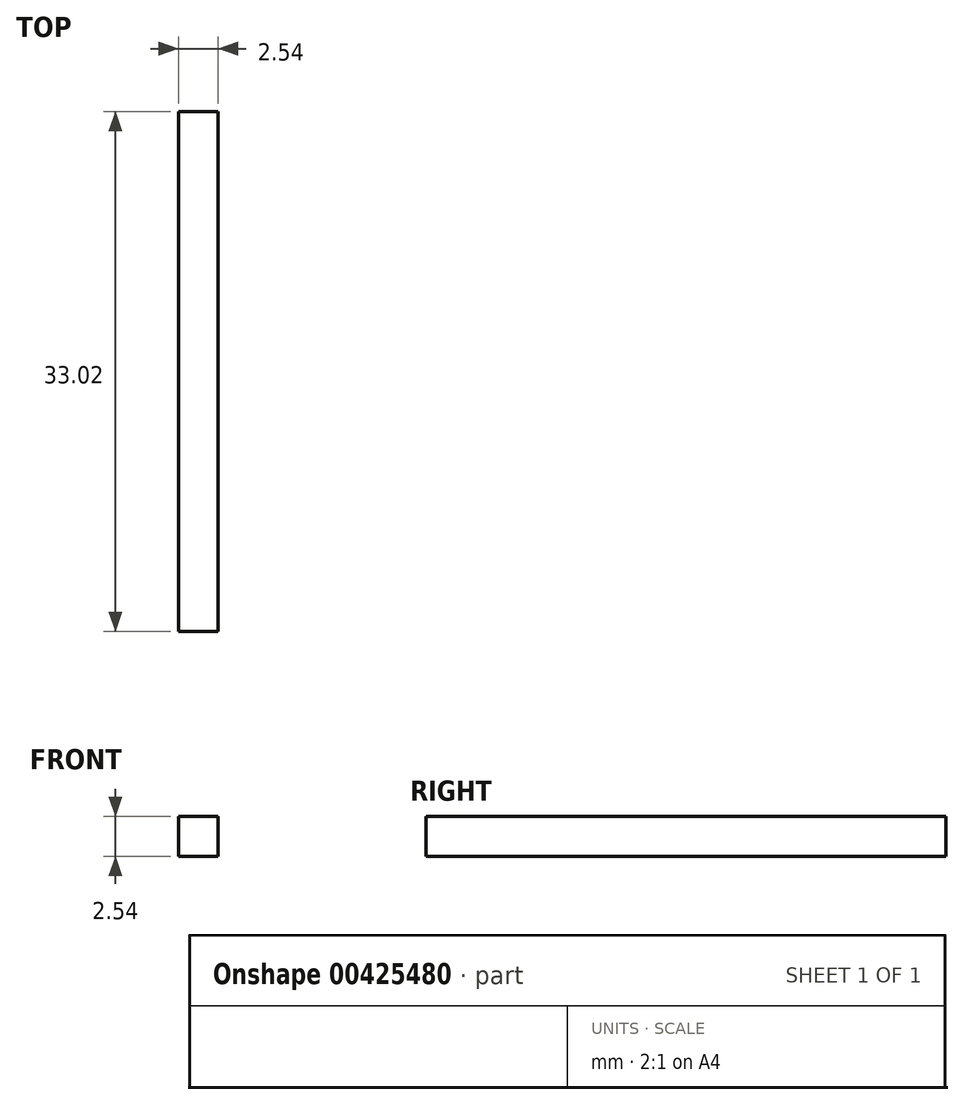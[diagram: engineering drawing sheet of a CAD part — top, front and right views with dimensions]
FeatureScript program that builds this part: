
annotation { "Feature Type Name" : "Feature", "Feature Type Description" : "" }
export const myFeature = defineFeature(function(context is Context, id is Id, definition is map)
    precondition{}
    {
        {
            var Q0;
            Q0=qCreatedBy(makeId("Right.planeOp"),FACE);
            var sketch = newSketch(context, id + "F0", { "sketchPlane" : qUnion([Q0])});
            skLineSegment(sketch, "E0.bottom", {"start": v(-66.13, -16.66) * mm, "end": v(60.87, -16.66) * mm});
            skLineSegment(sketch, "E0.top", {"start": v(-66.13, 59.54) * mm, "end": v(60.87, 59.54) * mm});
            skLineSegment(sketch, "E0.left", {"start": v(-66.13, -16.66) * mm, "end": v(-66.13, 59.54) * mm});
            skLineSegment(sketch, "E0.right", {"start": v(60.87, -16.66) * mm, "end": v(60.87, 59.54) * mm});
            skLineSegment(sketch, "E1.bottom", {"start": v(-66.13, -16.66) * mm, "end": v(-30.57, -16.66) * mm});
            skLineSegment(sketch, "E1.top", {"start": v(-66.13, 46.84) * mm, "end": v(-30.57, 46.84) * mm});
            skLineSegment(sketch, "E1.left", {"start": v(-66.13, -16.66) * mm, "end": v(-66.13, 46.84) * mm});
            skLineSegment(sketch, "E1.right", {"start": v(-30.57, -16.66) * mm, "end": v(-30.57, 46.84) * mm});
            skLineSegment(sketch, "E2", {"start": v(-63.6, 46.84) * mm, "end": v(-63.6, -16.66) * mm});
            skLineSegment(sketch, "E3", {"start": v(-63.6, -14.12) * mm, "end": v(-30.57, -14.12) * mm});
            skSolve(sketch);
        }
        {
            var Q0;
            Q0=makeQuery(id+"F0.imprint","IMPRINT",FACE,{"disambiguationData":[TD([[makeQuery(id+"F0.imprint","IMPRINT",EDGE,{"derivedFrom":sQuery(id+"F0.wireOp",EDGE,"E0.bottom")}),1.0]])]});
            var Q1;
            {var subQ0=sQuery(id+"F0.wireOp",EDGE,"E1.left");Q1=makeQuery(id+"F0.imprint","IMPRINT",FACE,{"disambiguationData":[TD([[makeQuery(id+"F0.imprint","IMPRINT",EDGE,{"derivedFrom":subQ0}),-1.0]])]});}
            var Q2;
            {var subQ5=sQuery(id+"F0.wireOp",EDGE,"E3");Q2=makeQuery(id+"F0.imprint","IMPRINT",FACE,{"disambiguationData":[TD([[makeQuery(id+"F0.imprint","IMPRINT",EDGE,{"derivedFrom":subQ5}),-1.0]])]});}
            extrude(context, id + "F1", {"entities" : qUnion([Q0, Q1, Q2]), "depth" : 2.54 * mm});
        }
    });
